# Revit family: RN 81056 Optipress-Aquaplus-Gomito prolungato
name_source: partatom
category: Rohrformteile
units: mm (PartAtom-declared; Revit-internal decimal feet)

## family parameters
Arbeitsebenenbasiert = Nein
Beim Laden mit Abzugskörper schneiden = Nein
Bemaßung runder Anschluss = Durchmesser verwenden
Gemeinsam genutzt = Nein
Immer vertikal = Ja
Teiletyp = Nicht definiert

## types (3) — shared parameters
1.010.00.2 Number of the part of the guideline = 29
1.010.00.3 Issue date (month) of the guideline = 201308
1.010.00.4 Manufacturer name = R. Nussbaum AG
1.010.00.5 Revision date of the file = 20190521
1.100.00.4 Product designation = Fornitura
1.110.00.2 Index = 4
1.110.00.4 Product designation = Optipress
1.960/3L.00.8 Link (URL) = https://www.nussbaum.ch
29.700.00.4 Product name = Optipress-Aquaplus-Gomito prolungato, con dado di chiusura
29.700.00.5 Product identification = 2
29.700.00.6 Cross-sectional shape = 1
29.700.00.7 Nominal size system = DN
29.700.00.8 Nominal pressure system = PN
29.710.02.3 Designation = Optipress-Aquaplus-Gomito prolungato, con dado di chiusura, DN=12x15, L=61, Rp=½
29.710.02.4 Nominal pressure = 16
29.710.02.5 max. allowed overpressure [hPa] = 1600
29.710.02.7 max. allowed continuous operating pressure [hPa] = 1600
29.710.02.9 max. allowed continuous operating temperature [°C] = 95
CONNECTOR0_DIAMETER_dZ_0r = 12 mm  [stored 0.0393701 ft]
CONNECTOR0_dZ_00 = 61 mm
CONNECTOR0_dZ_01 = 39 mm
CONNECTOR0_ref_dZ = 39 mm
CONNECTOR1_DIAMETER_dX_0r = 15 mm
Connector Visibility = Nein
EnclosingSpace Visibility = Nein

## per-type parameters (varying)
| type | 1.800.00.3 BS number | 1.810.00.3 Manufacturer’s reference number | 1.810.00.4 DATANORM number | 1.810.00.5 StLB number | 1.810.00.6 GTIN number | 29.710.02.10 Fitting weight [kg] | CONNECTOR1_dX_00 | CONNECTOR1_dX_01 | CONNECTOR1_ref_dX | R. Nussbaum AG 81056.21 it Visibility | R. Nussbaum AG 81056.22 it Visibility | R. Nussbaum AG 81056.23 it Visibility |
| 81056.21, Optipress-Aquaplus-Gomito prolungato, con dado di chiusura, DN=12x15, L=61, Rp=½ | 01900400000000000000000000000000000000000000000045000000000000000001 | 81056.21 | 81056.21 | 263.212 | 7612945022660 | 0.21 | 10 mm  [stored 0.0328084 ft] | 45 mm | 10 mm  [stored 0.0328084 ft] | Ja | Nein | Nein |
| 81056.22, Optipress-Aquaplus-Gomito prolungato, con dado di chiusura, DN=12x15, L=61, Rp=½ | 01900400000000000000000000000000000000000000000045000000000000000002 | 81056.22 | 81056.22 |  | 7612945022677 | 0.315 | 25 mm  [stored 0.082021 ft] | 90 mm | 25 mm  [stored 0.082021 ft] | Nein | Ja | Nein |
| 81056.23, Optipress-Aquaplus-Gomito prolungato, con dado di chiusura, DN=12x15, L=61, Rp=½ | 01900400000000000000000000000000000000000000000045000000000000000003 | 81056.23 | 81056.23 |  | 7612945022684 | 0.459 | 70 mm | 150 mm | 70 mm | Nein | Nein | Ja |

note: column(s) folded — value = type name in every type: 1.800.00.4 Comment field

note: [stored X ft] marks values corroborated as IEEE doubles in the binary element streams (Revit-internal decimal feet)

## geometry (parser evidence)
native form markers: Sweep x3
no freeform markers — native parametric forms only
